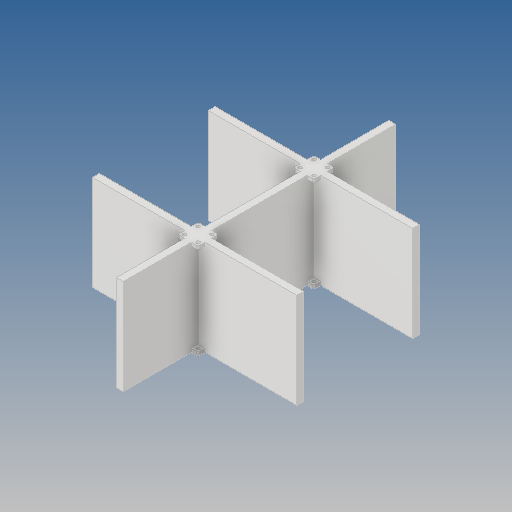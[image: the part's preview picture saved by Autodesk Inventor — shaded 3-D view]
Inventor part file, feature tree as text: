
AUTODESK INVENTOR PART (.ipt)
format: ipt  version: 2020 (Build 240168000, 168)  size: 278,016 bytes
history: native  units: mm
features: other x3, extrude x3, sketch x2, mirror x1, projected_geometry x1
ambient origin geometry x8: Origin, YZ Plane, XZ Plane, XY Plane, X Axis, Y Axis, Z Axis, Center Point
bodies: Body1 (feature_tree)
feature tree (10):
  other  "крепление-стенки"
  other  "Твердое тело1"
  sketch  "Эскиз1"
  extrude  "Выдавливание1"  Depth=120.0mm
  other  "РабПлоскость1"
  extrude  "Выдавливание2"  Depth=4.0mm
  mirror  "Зеркальное отражение1"
  extrude  "Выдавливание3"  Depth=4.0mm
  sketch  "Эскиз2"
  projected_geometry  "Спроецированная петля1"
